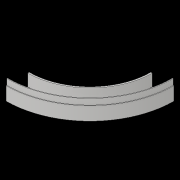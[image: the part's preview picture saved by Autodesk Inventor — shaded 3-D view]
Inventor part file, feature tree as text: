
AUTODESK INVENTOR PART (.ipt)
format: ipt  version: 2017 (Build 210142000, 142)  size: 120,320 bytes
history: native  units: in
note: dims shown in document units (in); Inventor stores cm internally (conversion verified against a paired STEP export)
features: sketch x2, revolve x1, extrude x1
ambient origin geometry x8: Origin, YZ Plane, XZ Plane, XY Plane, X Axis, Y Axis, Z Axis, Center Point
bodies: Solid1 (feature_tree)
feature tree (4):
  revolve  "Revolution1"  [1 undecoded]
  extrude  "Extrusion1"  Depth=0.125in
  sketch  "Sketch1"  dims[d0=2.0in d2=10.5in]
  sketch  "Sketch2"  dims[d3=2.0in d4=2.875in d5=0.125in d6=0.125in d7=0.125in d8=0.125in d9=0.125in d10=0.125in d11=0.125in d12=0.125in d13=1.0285in d14=0.5in d15=180.0deg d16=5.25in d17=0.125in d18=0.125in d19=0.25in d20=0.0625in d21=0.25in d22=0.25in d23=1.0in d24=0.0in]
note: 1 required parameter value undecoded (feature->parameter linkage not recoverable at this tier; creation-order binding heuristic only, values carry confidence <= 0.55)
